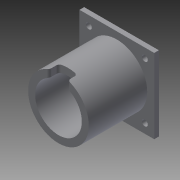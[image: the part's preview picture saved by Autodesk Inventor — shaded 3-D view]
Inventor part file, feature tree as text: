
AUTODESK INVENTOR PART (.ipt)
format: ipt  version: 2015 (Build 190159000, 159)  size: 166,912 bytes
history: native  units: in
note: dims shown in document units (in); Inventor stores cm internally (conversion verified against a paired STEP export)
features: sketch x6, extrude x5, hole x1, plane x1, fillet x1
ambient origin geometry x8: Origin, YZ Plane, XZ Plane, XY Plane, X Axis, Y Axis, Z Axis, Center Point
bodies: Solid1 (feature_tree)
feature tree (14):
  extrude  "Extrusion1"  Depth=1.6in
  extrude  "Extrusion2"  Depth=0.8in
  hole  "Hole1"  [1 undecoded]
  plane  "Work Plane1"
  extrude  "Extrusion3"  Depth=1.25in TaperAngle=0.0deg
  extrude  "Extrusion4"  Depth=0.2in
  fillet  "Fillet1"  Radius=0.2in
  extrude  "Extrusion5"  Depth=0.3in
  sketch  "Sketch1"  dims[d0=1.6in d1=1.6in]
  sketch  "Sketch2"  dims[d2=0.8in d3=0.8in]
  sketch  "Sketch3"  dims[d4=0.1in d5=0.0in d6=1.0in]
  sketch  "Sketch4"  dims[d7=0.15in d8=1.25in d9=0.0in]
  sketch  "Sketch5"  dims[d10=0.2in d11=0.2in d12=0.2in]
  sketch  "Sketch6"  dims[d13=0.2in d14=0.2in d15=0.2in d16=0.2in d17=0.2in d18=0.125in d19=0.75in d20=0.375in d21=0.25in d22=0.5635in d23=0.125in d24=0.8108in d25=0.65in d26=0.2in d27=0.4in d28=0.2in d29=0.4in d30=0.0in d31=0.35in d32=0.4in d33=0.0in d34=0.05in d35=0.642in d36=0.3in d37=0.3in d38=0.125in d39=0.3in d41=0.9in d42=0.125in d43=1.0in d44=0.0in]
note: 1 required parameter value undecoded (feature->parameter linkage not recoverable at this tier; creation-order binding heuristic only, values carry confidence <= 0.55)
